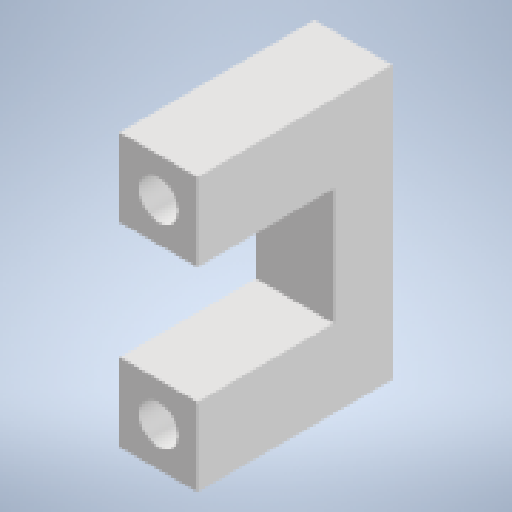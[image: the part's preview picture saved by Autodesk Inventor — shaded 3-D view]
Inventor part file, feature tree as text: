
AUTODESK INVENTOR PART (.ipt)
format: ipt  version: 2024.2 (Build 282272000, 272)  size: 136,192 bytes
history: native  units: mm
features: extrude x2, sketch x2, other x1
ambient origin geometry x8: Origin, YZ Plane, XZ Plane, XY Plane, X Axis, Y Axis, Z Axis, Center Point
bodies: Body1 (feature_tree)
feature tree (5):
  other  "Твердое тело1"
  extrude  "Выдавливание1"  Depth=2.0mm
  extrude  "Выдавливание2"  Depth=2.0mm
  sketch  "Эскиз1"
  sketch  "Эскиз2"
